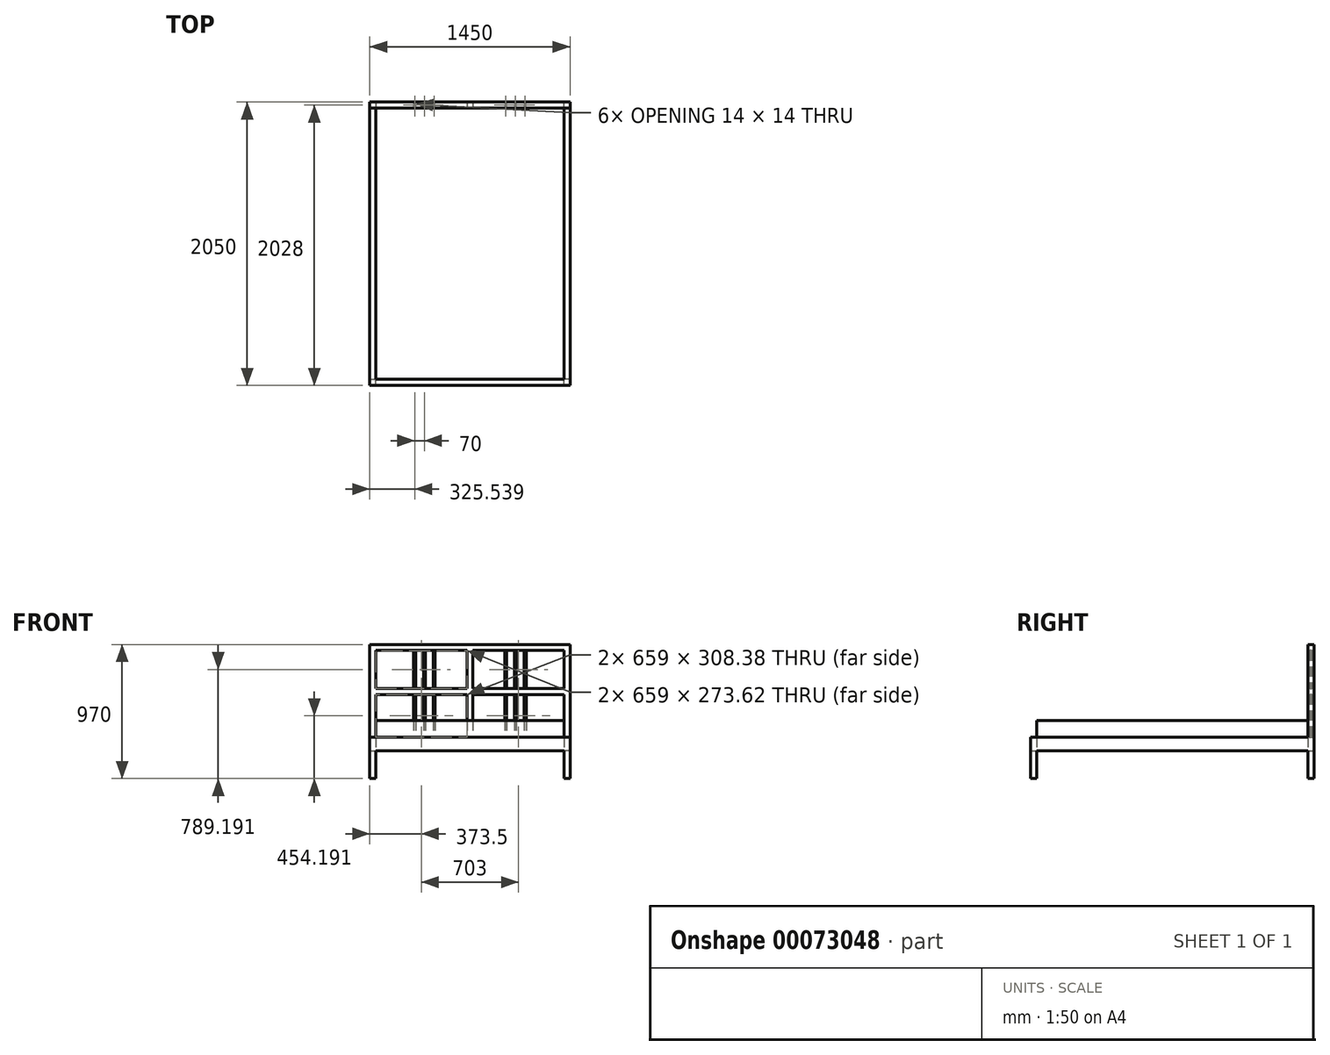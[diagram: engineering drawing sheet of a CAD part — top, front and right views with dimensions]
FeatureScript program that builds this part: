
annotation { "Feature Type Name" : "Feature", "Feature Type Description" : "" }
export const myFeature = defineFeature(function(context is Context, id is Id, definition is map)
    precondition{}
    {
        {
            var Q0;
            Q0=qCreatedBy(makeId("Top.planeOp"),FACE);
            var sketch = newSketch(context, id + "F0", { "sketchPlane" : qUnion([Q0])});
            skLineSegment(sketch, "E0.bottom", {"start": v(0, 0) * mm, "end": v(1450, 0) * mm});
            skLineSegment(sketch, "E0.top", {"start": v(0, -2050) * mm, "end": v(1450, -2050) * mm});
            skLineSegment(sketch, "E0.left", {"start": v(0, 0) * mm, "end": v(0, -2050) * mm});
            skLineSegment(sketch, "E0.right", {"start": v(1450, 0) * mm, "end": v(1450, -2050) * mm});
            skLineSegment(sketch, "E1.0", {"start": v(1406, -44) * mm, "end": v(1406, -2006) * mm});
            skLineSegment(sketch, "E1.1", {"start": v(44, -44) * mm, "end": v(1406, -44) * mm});
            skLineSegment(sketch, "E1.2", {"start": v(44, -44) * mm, "end": v(44, -2006) * mm});
            skLineSegment(sketch, "E1.3", {"start": v(44, -2006) * mm, "end": v(1406, -2006) * mm});
            skSolve(sketch);
        }
        {
            var Q0;
            Q0=makeQuery(id+"F0.imprint","IMPRINT",FACE,{"disambiguationData":[TD([[makeQuery(id+"F0.imprint","IMPRINT",EDGE,{"derivedFrom":sQuery(id+"F0.wireOp",EDGE,"E0.bottom")}),-1.0]])]});
            extrude(context, id + "F1", {"entities" : qUnion([Q0]), "depth" : 100 * mm});
        }
        {
            var Q0;
            Q0=makeQuery(id+"F1.opExtrude","CAP_FACE",FACE,{"disambiguationData":[OSD([sQuery(id+"F0.wireOp",EDGE,"E0.bottom"),sQuery(id+"F0.wireOp",EDGE,"E0.top"),sQuery(id+"F0.wireOp",EDGE,"E0.left"),sQuery(id+"F0.wireOp",EDGE,"E0.right"),sQuery(id+"F0.wireOp",EDGE,"E1.0"),sQuery(id+"F0.wireOp",EDGE,"E1.1"),sQuery(id+"F0.wireOp",EDGE,"E1.2"),sQuery(id+"F0.wireOp",EDGE,"E1.3")])],"isStart":false});
            var sketch = newSketch(context, id + "F2", { "sketchPlane" : qUnion([Q0])});
            skLineSegment(sketch, "E2.bottom", {"start": v(1406, -44) * mm, "end": v(1450, -44) * mm});
            skLineSegment(sketch, "E2.top", {"start": v(1406, 0) * mm, "end": v(1450, 0) * mm});
            skLineSegment(sketch, "E2.left", {"start": v(1406, -44) * mm, "end": v(1406, 0) * mm});
            skLineSegment(sketch, "E2.right", {"start": v(1450, -44) * mm, "end": v(1450, 0) * mm});
            skLineSegment(sketch, "E3.bottom", {"start": v(44, -44) * mm, "end": v(0, -44) * mm});
            skLineSegment(sketch, "E3.top", {"start": v(44, 0) * mm, "end": v(0, 0) * mm});
            skLineSegment(sketch, "E3.left", {"start": v(44, -44) * mm, "end": v(44, 0) * mm});
            skLineSegment(sketch, "E3.right", {"start": v(0, -44) * mm, "end": v(0, 0) * mm});
            skLineSegment(sketch, "E4.bottom", {"start": v(747, -44) * mm, "end": v(703, -44) * mm});
            skLineSegment(sketch, "E4.top", {"start": v(747, 0) * mm, "end": v(703, 0) * mm});
            skLineSegment(sketch, "E4.left", {"start": v(747, -44) * mm, "end": v(747, 0) * mm});
            skLineSegment(sketch, "E4.right", {"start": v(703, -44) * mm, "end": v(703, 0) * mm});
            skLineSegment(sketch, "E5", {"start": v(725, 0) * mm, "end": v(725, -44) * mm, "construction": true});
            skCircle(sketch, "E6", {"center": v(1054.46, -22) * mm, "radius": 7 * mm});
            skCircle(sketch, "E7", {"center": v(984.46, -22) * mm, "radius": 7 * mm});
            skCircle(sketch, "E8", {"center": v(1124.46, -22) * mm, "radius": 7 * mm});
            skLineSegment(sketch, "E9", {"start": v(984.46, -22) * mm, "end": v(1124.46, -22) * mm, "construction": true});
            skCircle(sketch, "E10.MirrorC", {"center": v(465.54, -22) * mm, "radius": 7 * mm});
            skCircle(sketch, "E11.MirrorC", {"center": v(395.54, -22) * mm, "radius": 7 * mm});
            skCircle(sketch, "E12.MirrorC", {"center": v(325.54, -22) * mm, "radius": 7 * mm});
            skSolve(sketch);
        }
        {
            var Q0;
            Q0 = qSketchRegion(id + "F2", true);
            extrude(context, id + "F3", {"entities" : qUnion([Q0]), "operationType" : NewBodyOperationType.ADD, "depth" : 670 * mm});
        }
        {
            var Q0;
            Q0=makeQuery(id+"F3.opExtrude","SWEPT_FACE",FACE,{"disambiguationData":[OSD([sQuery(id+"F2.wireOp",EDGE,"E3.left")])]});
            var sketch = newSketch(context, id + "F4", { "sketchPlane" : qUnion([Q0])});
            skLineSegment(sketch, "E13.bottom", {"start": v(-44, 770) * mm, "end": v(0, 770) * mm});
            skLineSegment(sketch, "E13.top", {"start": v(-44, 726) * mm, "end": v(0, 726) * mm});
            skLineSegment(sketch, "E13.left", {"start": v(-44, 770) * mm, "end": v(-44, 726) * mm});
            skLineSegment(sketch, "E13.right", {"start": v(0, 770) * mm, "end": v(0, 726) * mm});
            skLineSegment(sketch, "E14.bottom", {"start": v(0, 452.38) * mm, "end": v(-44, 452.38) * mm});
            skLineSegment(sketch, "E14.top", {"start": v(0, 408.38) * mm, "end": v(-44, 408.38) * mm});
            skLineSegment(sketch, "E14.left", {"start": v(0, 452.38) * mm, "end": v(0, 408.38) * mm});
            skLineSegment(sketch, "E14.right", {"start": v(-44, 452.38) * mm, "end": v(-44, 408.38) * mm});
            skSolve(sketch);
        }
        {
            var Q0;
            Q0 = qSketchRegion(id + "F4", true);
            var Q1;
            Q1=makeQuery(id+"F3.opExtrude","SWEPT_FACE",FACE,{"disambiguationData":[OSD([sQuery(id+"F2.wireOp",EDGE,"E2.left")])]});
            extrude(context, id + "F5", {"entities" : qUnion([Q0]), "operationType" : NewBodyOperationType.ADD, "endBound" : BoundingType.UP_TO_SURFACE, "endBoundEntityFace" : qUnion([Q1]), "depth" : 25 * mm});
        }
        {
            var Q0;
            Q0=makeQuery(id+"F0.imprint","IMPRINT",FACE,{"disambiguationData":[TD([[makeQuery(id+"F0.imprint","IMPRINT",EDGE,{"derivedFrom":sQuery(id+"F0.wireOp",EDGE,"E0.bottom")}),-1.0]])]});
            var sketch = newSketch(context, id + "F6", { "sketchPlane" : qUnion([Q0])});
            skLineSegment(sketch, "E15.bottom", {"start": v(0, 0) * mm, "end": v(44, 0) * mm});
            skLineSegment(sketch, "E15.top", {"start": v(0, -44) * mm, "end": v(44, -44) * mm});
            skLineSegment(sketch, "E15.left", {"start": v(0, 0) * mm, "end": v(0, -44) * mm});
            skLineSegment(sketch, "E15.right", {"start": v(44, 0) * mm, "end": v(44, -44) * mm});
            skLineSegment(sketch, "E16.bottom", {"start": v(1406, -44) * mm, "end": v(1450, -44) * mm});
            skLineSegment(sketch, "E16.top", {"start": v(1406, 0) * mm, "end": v(1450, 0) * mm});
            skLineSegment(sketch, "E16.left", {"start": v(1406, -44) * mm, "end": v(1406, 0) * mm});
            skLineSegment(sketch, "E16.right", {"start": v(1450, -44) * mm, "end": v(1450, 0) * mm});
            skLineSegment(sketch, "E17.bottom", {"start": v(1450, -2050) * mm, "end": v(1406, -2050) * mm});
            skLineSegment(sketch, "E17.top", {"start": v(1450, -2006) * mm, "end": v(1406, -2006) * mm});
            skLineSegment(sketch, "E17.left", {"start": v(1450, -2050) * mm, "end": v(1450, -2006) * mm});
            skLineSegment(sketch, "E17.right", {"start": v(1406, -2050) * mm, "end": v(1406, -2006) * mm});
            skLineSegment(sketch, "E18.bottom", {"start": v(0, -2050) * mm, "end": v(44, -2050) * mm});
            skLineSegment(sketch, "E18.top", {"start": v(0, -2006) * mm, "end": v(44, -2006) * mm});
            skLineSegment(sketch, "E18.left", {"start": v(0, -2050) * mm, "end": v(0, -2006) * mm});
            skLineSegment(sketch, "E18.right", {"start": v(44, -2050) * mm, "end": v(44, -2006) * mm});
            skSolve(sketch);
        }
        {
            var Q0;
            Q0 = qSketchRegion(id + "F6", true);
            extrude(context, id + "F7", {"entities" : qUnion([Q0]), "operationType" : NewBodyOperationType.ADD, "oppositeDirection" : true, "depth" : 200 * mm});
        }
        {
            var Q0;
            Q0=makeQuery(id+"F0.imprint","IMPRINT",FACE,{"disambiguationData":[TD([[makeQuery(id+"F0.imprint","IMPRINT",EDGE,{"derivedFrom":sQuery(id+"F0.wireOp",EDGE,"E1.0")}),-1.0]])]});
            extrude(context, id + "F8", {"entities" : qUnion([Q0]), "depth" : 220 * mm});
        }
    });
